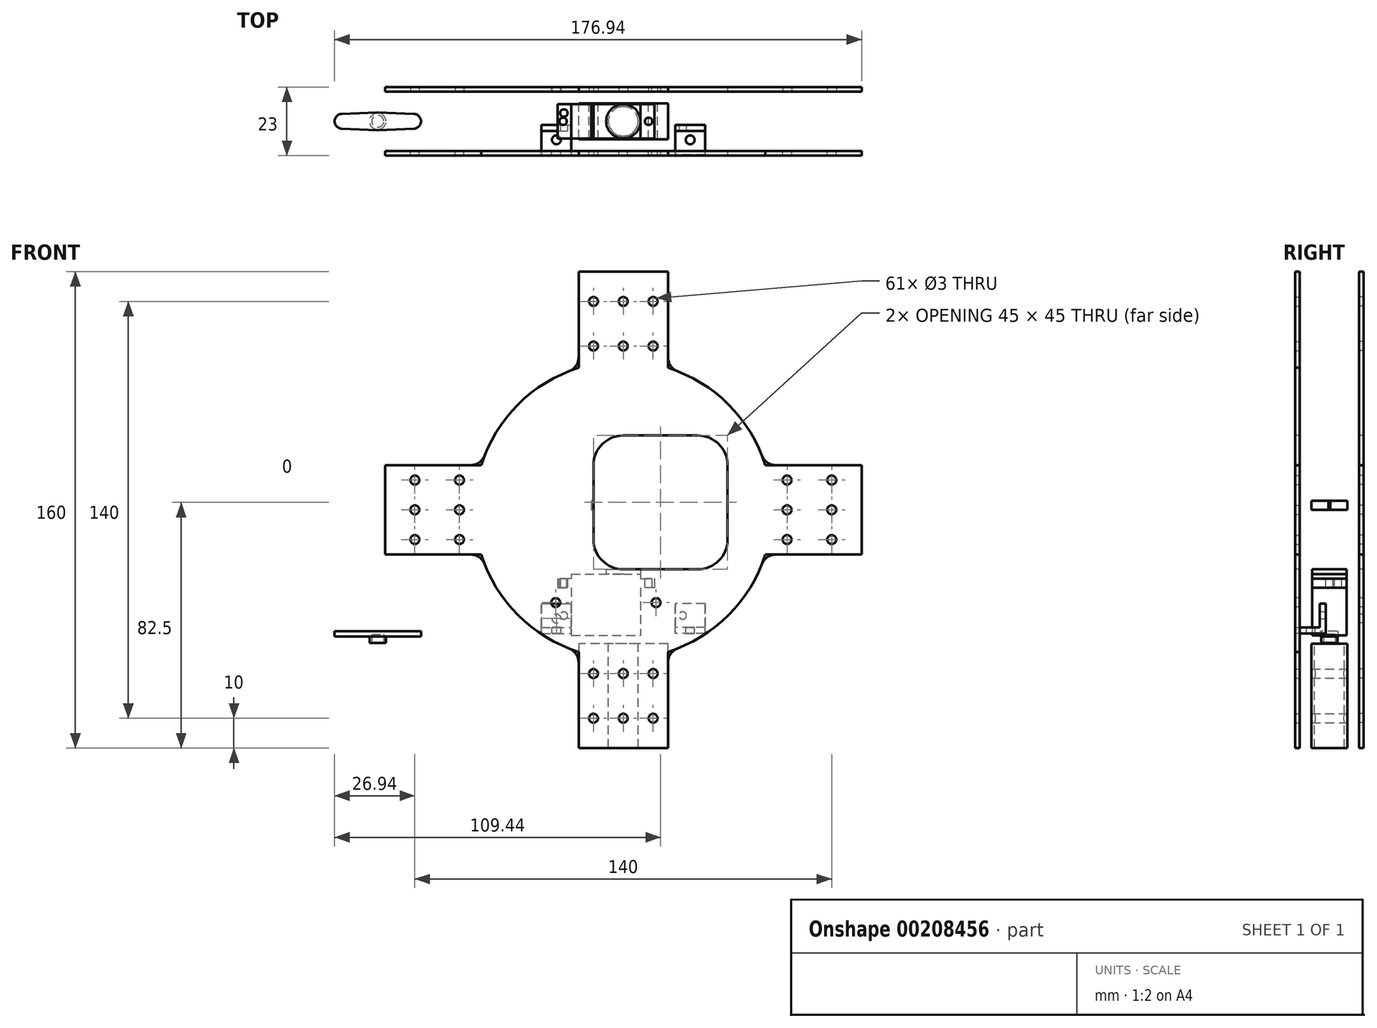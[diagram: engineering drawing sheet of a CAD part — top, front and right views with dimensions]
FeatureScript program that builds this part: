
annotation { "Feature Type Name" : "Feature", "Feature Type Description" : "" }
export const myFeature = defineFeature(function(context is Context, id is Id, definition is map)
    precondition{}
    {
        {
            var Q0;
            Q0=qCreatedBy(makeId("Top.planeOp"),FACE);
            var sketch = newSketch(context, id + "F0", { "sketchPlane" : qUnion([Q0])});
            skCircle(sketch, "E0", {"center": v(0, 0) * mm, "radius": 6 * mm});
            skLineSegment(sketch, "E1.bottom", {"start": v(-10.8, 6) * mm, "end": v(21.6, 6) * mm});
            skLineSegment(sketch, "E1.top", {"start": v(-10.8, -6) * mm, "end": v(21.6, -6) * mm});
            skLineSegment(sketch, "E1.left", {"start": v(-10.8, 6) * mm, "end": v(-10.8, -6) * mm});
            skLineSegment(sketch, "E1.right", {"start": v(21.6, 6) * mm, "end": v(21.6, -6) * mm});
            skCircle(sketch, "E2", {"center": v(-8.8, 0) * mm, "radius": 1.25 * mm});
            skCircle(sketch, "E3", {"center": v(19.6, 0) * mm, "radius": 1.25 * mm});
            skLineSegment(sketch, "E4", {"start": v(-6, 6) * mm, "end": v(-6, -6) * mm});
            skLineSegment(sketch, "E5", {"start": v(16.8, 6) * mm, "end": v(16.8, -6) * mm});
            skLineSegment(sketch, "E6", {"start": v(5.4, 6) * mm, "end": v(5.4, -6) * mm, "construction": true});
            skCircle(sketch, "E7", {"center": v(0, 0) * mm, "radius": 2 * mm});
            skSolve(sketch);
        }
        {
            var Q0;
            {var subQ5=sQuery(id+"F0.wireOp",EDGE,"E5");Q0=makeQuery(id+"F0.imprint","IMPRINT",FACE,{"disambiguationData":[TD([[makeQuery(id+"F0.imprint","IMPRINT",EDGE,{"derivedFrom":subQ5}),-1.0]])]});}
            var Q1;
            {var subQ0=sQuery(id+"F0.wireOp",EDGE,"E1.bottom");var subQ1=sQuery(id+"F0.wireOp",EDGE,"E0");var subQ2=makeQuery(id+"F0.imprint","INTERSECT",VERTEX,{"derivedFrom":[subQ1,subQ0]});Q1=makeQuery(id+"F0.imprint","IMPRINT",FACE,{"disambiguationData":[TD([[makeQuery(id+"F0.imprint","IMPRINT",EDGE,{"disambiguationData":[TD([[subQ2,-1.0]])],"derivedFrom":subQ1}),-1.0]])]});}
            var Q2;
            {var subQ0=sQuery(id+"F0.wireOp",EDGE,"E1.top");var subQ1=sQuery(id+"F0.wireOp",EDGE,"E0");var subQ2=makeQuery(id+"F0.imprint","INTERSECT",VERTEX,{"derivedFrom":[subQ1,subQ0]});Q2=makeQuery(id+"F0.imprint","IMPRINT",FACE,{"disambiguationData":[TD([[makeQuery(id+"F0.imprint","IMPRINT",EDGE,{"disambiguationData":[TD([[subQ2,1.0]])],"derivedFrom":subQ1}),-1.0]])]});}
            var Q3;
            {var subQ0=sQuery(id+"F0.wireOp",EDGE,"E0");var subQ1=makeQuery(id+"F0.imprint","INTERSECT",VERTEX,{"derivedFrom":[subQ0,sQuery(id+"F0.wireOp",EDGE,"E1.bottom")]});Q3=makeQuery(id+"F0.imprint","IMPRINT",FACE,{"disambiguationData":[TD([[makeQuery(id+"F0.imprint","IMPRINT",EDGE,{"disambiguationData":[TD([[subQ1,-1.0]])],"derivedFrom":subQ0}),1.0]])]});}
            var Q4;
            Q4=makeQuery(id+"F0.imprint","IMPRINT",FACE,{"disambiguationData":[TD([[makeQuery(id+"F0.imprint","IMPRINT",EDGE,{"derivedFrom":sQuery(id+"F0.wireOp",EDGE,"E7")}),1.0]])]});
            extrude(context, id + "F1", {"entities" : qUnion([Q0, Q1, Q2, Q3, Q4]), "oppositeDirection" : true, "depth" : 3 * mm});
        }
        {
            var Q0;
            {var subQ0=sQuery(id+"F0.wireOp",EDGE,"E1.left");Q0=makeQuery(id+"F0.imprint","IMPRINT",FACE,{"disambiguationData":[TD([[makeQuery(id+"F0.imprint","IMPRINT",EDGE,{"derivedFrom":subQ0}),1.0]])]});}
            var Q1;
            {var subQ0=sQuery(id+"F0.wireOp",EDGE,"E1.right");Q1=makeQuery(id+"F0.imprint","IMPRINT",FACE,{"disambiguationData":[TD([[makeQuery(id+"F0.imprint","IMPRINT",EDGE,{"derivedFrom":subQ0}),-1.0]])]});}
            var Q2;
            {var subQ5=sQuery(id+"F0.wireOp",EDGE,"E5");Q2=makeQuery(id+"F0.imprint","IMPRINT",FACE,{"disambiguationData":[TD([[makeQuery(id+"F0.imprint","IMPRINT",EDGE,{"derivedFrom":subQ5}),-1.0]])]});}
            var Q3;
            {var subQ0=sQuery(id+"F0.wireOp",EDGE,"E1.top");var subQ1=sQuery(id+"F0.wireOp",EDGE,"E0");var subQ2=makeQuery(id+"F0.imprint","INTERSECT",VERTEX,{"derivedFrom":[subQ1,subQ0]});Q3=makeQuery(id+"F0.imprint","IMPRINT",FACE,{"disambiguationData":[TD([[makeQuery(id+"F0.imprint","IMPRINT",EDGE,{"disambiguationData":[TD([[subQ2,1.0]])],"derivedFrom":subQ1}),-1.0]])]});}
            var Q4;
            {var subQ0=sQuery(id+"F0.wireOp",EDGE,"E0");var subQ1=makeQuery(id+"F0.imprint","INTERSECT",VERTEX,{"derivedFrom":[subQ0,sQuery(id+"F0.wireOp",EDGE,"E1.bottom")]});Q4=makeQuery(id+"F0.imprint","IMPRINT",FACE,{"disambiguationData":[TD([[makeQuery(id+"F0.imprint","IMPRINT",EDGE,{"disambiguationData":[TD([[subQ1,-1.0]])],"derivedFrom":subQ0}),1.0]])]});}
            var Q5;
            {var subQ0=sQuery(id+"F0.wireOp",EDGE,"E1.bottom");var subQ1=sQuery(id+"F0.wireOp",EDGE,"E0");var subQ2=makeQuery(id+"F0.imprint","INTERSECT",VERTEX,{"derivedFrom":[subQ1,subQ0]});Q5=makeQuery(id+"F0.imprint","IMPRINT",FACE,{"disambiguationData":[TD([[makeQuery(id+"F0.imprint","IMPRINT",EDGE,{"disambiguationData":[TD([[subQ2,-1.0]])],"derivedFrom":subQ1}),-1.0]])]});}
            var Q6;
            Q6=makeQuery(id+"F0.imprint","IMPRINT",FACE,{"disambiguationData":[TD([[makeQuery(id+"F0.imprint","IMPRINT",EDGE,{"derivedFrom":sQuery(id+"F0.wireOp",EDGE,"E7")}),1.0]])]});
            extrude(context, id + "F2", {"entities" : qUnion([Q0, Q1, Q2, Q3, Q4, Q5, Q6]), "operationType" : NewBodyOperationType.ADD, "depth" : 3 * mm});
        }
        {
            var Q0;
            {var subQ0=sQuery(id+"F0.wireOp",EDGE,"E0");var subQ1=makeQuery(id+"F0.imprint","INTERSECT",VERTEX,{"derivedFrom":[subQ0,sQuery(id+"F0.wireOp",EDGE,"E1.bottom")]});Q0=makeQuery(id+"F0.imprint","IMPRINT",FACE,{"disambiguationData":[TD([[makeQuery(id+"F0.imprint","IMPRINT",EDGE,{"disambiguationData":[TD([[subQ1,-1.0]])],"derivedFrom":subQ0}),1.0]])]});}
            var Q1;
            Q1=makeQuery(id+"F0.imprint","IMPRINT",FACE,{"disambiguationData":[TD([[makeQuery(id+"F0.imprint","IMPRINT",EDGE,{"derivedFrom":sQuery(id+"F0.wireOp",EDGE,"E7")}),1.0]])]});
            extrude(context, id + "F3", {"entities" : qUnion([Q0, Q1]), "operationType" : NewBodyOperationType.ADD, "depth" : (25.4 - 16.82) * mm});
        }
        {
            var Q0;
            Q0=qCreatedBy(makeId("Front.planeOp"),FACE);
            var sketch = newSketch(context, id + "F4", { "sketchPlane" : qUnion([Q0])});
            skLineSegment(sketch, "E8", {"start": v(-6, 3) * mm, "end": v(-6, 5.5) * mm});
            skLineSegment(sketch, "E9", {"start": v(-6, 5.5) * mm, "end": v(0, 7) * mm});
            skLineSegment(sketch, "E10", {"start": v(0, 7) * mm, "end": v(16.8, 3) * mm});
            skLineSegment(sketch, "E11", {"start": v(16.8, 3) * mm, "end": v(-6, 3) * mm});
            skSolve(sketch);
        }
        {
            var Q0;
            Q0 = qSketchRegion(id + "F4", true);
            var Q1;
            {var subQ0=sQuery(id+"F0.wireOp",EDGE,"E1.top");Q1=makeQuery(id+"F2.boolean.opBoolean","MERGE",FACE,{"derivedFrom":[makeQuery(id+"F1.opExtrude","SWEPT_FACE",FACE,{"disambiguationData":[OSD([subQ0])]}),makeQuery(id+"F2.opExtrude","SWEPT_FACE",FACE,{"disambiguationData":[OSD([subQ0])]})]});}
            var Q2;
            {var subQ0=sQuery(id+"F0.wireOp",EDGE,"E1.bottom");Q2=makeQuery(id+"F2.boolean.opBoolean","MERGE",FACE,{"derivedFrom":[makeQuery(id+"F1.opExtrude","SWEPT_FACE",FACE,{"disambiguationData":[OSD([subQ0])]}),makeQuery(id+"F2.opExtrude","SWEPT_FACE",FACE,{"disambiguationData":[OSD([subQ0])]})]});}
            extrude(context, id + "F5", {"entities" : qUnion([Q0]), "operationType" : NewBodyOperationType.ADD, "endBound" : BoundingType.UP_TO_SURFACE, "endBoundEntityFace" : qUnion([Q1]), "depth" : 25 * mm, "hasSecondDirection" : true, "secondDirectionBound" : SecondDirectionBoundingType.UP_TO_SURFACE, "secondDirectionOppositeDirection" : true, "secondDirectionBoundEntityFace" : qUnion([Q2]), "secondDirectionDepth" : 25 * mm});
        }
        {
            var Q0;
            Q0=makeQuery(id+"F0.imprint","IMPRINT",FACE,{"disambiguationData":[TD([[makeQuery(id+"F0.imprint","IMPRINT",EDGE,{"derivedFrom":sQuery(id+"F0.wireOp",EDGE,"E7")}),1.0]])]});
            extrude(context, id + "F6", {"entities" : qUnion([Q0]), "operationType" : NewBodyOperationType.ADD, "depth" : 11.48 * mm});
        }
        {
            var Q0;
            Q0=makeQuery(id+"F2.opExtrude","SWEPT_EDGE",EDGE,{"disambiguationData":[OSD([sQuery(id+"F0.wireOp",EDGE,"E1.top"),sQuery(id+"F0.wireOp",EDGE,"E1.right")])]});
            var Q1;
            Q1=makeQuery(id+"F1.opExtrude","SWEPT_EDGE",EDGE,{"disambiguationData":[OSD([sQuery(id+"F0.wireOp",EDGE,"E1.top"),sQuery(id+"F0.wireOp",EDGE,"E5")])]});
            var Q2;
            Q2=makeQuery(id+"F2.opExtrude","SWEPT_EDGE",EDGE,{"disambiguationData":[OSD([sQuery(id+"F0.wireOp",EDGE,"E1.bottom"),sQuery(id+"F0.wireOp",EDGE,"E1.right")])]});
            var Q3;
            Q3=makeQuery(id+"F1.opExtrude","SWEPT_EDGE",EDGE,{"disambiguationData":[OSD([sQuery(id+"F0.wireOp",EDGE,"E1.bottom"),sQuery(id+"F0.wireOp",EDGE,"E5")])]});
            var Q4;
            Q4=makeQuery(id+"F1.opExtrude","SWEPT_EDGE",EDGE,{"disambiguationData":[OSD([sQuery(id+"F0.wireOp",EDGE,"E1.top"),sQuery(id+"F0.wireOp",EDGE,"E4")])]});
            var Q5;
            {var subQ0=sQuery(id+"F0.wireOp",EDGE,"E1.top");Q5=makeQuery(id+"F5.opExtrude","TWEAK_EDGE",EDGE,{"derivedFrom":[makeQuery(id+"F2.boolean.opBoolean","MERGE",FACE,{"derivedFrom":[makeQuery(id+"F1.opExtrude","SWEPT_FACE",FACE,{"disambiguationData":[OSD([subQ0])]}),makeQuery(id+"F2.opExtrude","SWEPT_FACE",FACE,{"disambiguationData":[OSD([subQ0])]})]}),makeQuery(id+"F4.imprint","IMPRINT",EDGE,{"derivedFrom":sQuery(id+"F4.wireOp",EDGE,"E8")})]});}
            var Q6;
            Q6=makeQuery(id+"F2.opExtrude","SWEPT_EDGE",EDGE,{"disambiguationData":[OSD([sQuery(id+"F0.wireOp",EDGE,"E1.top"),sQuery(id+"F0.wireOp",EDGE,"E1.left")])]});
            var Q7;
            Q7=makeQuery(id+"F2.opExtrude","SWEPT_EDGE",EDGE,{"disambiguationData":[OSD([sQuery(id+"F0.wireOp",EDGE,"E1.bottom"),sQuery(id+"F0.wireOp",EDGE,"E1.left")])]});
            var Q8;
            Q8=makeQuery(id+"F1.opExtrude","SWEPT_EDGE",EDGE,{"disambiguationData":[OSD([sQuery(id+"F0.wireOp",EDGE,"E1.bottom"),sQuery(id+"F0.wireOp",EDGE,"E4")])]});
            var Q9;
            {var subQ0=sQuery(id+"F0.wireOp",EDGE,"E1.bottom");Q9=makeQuery(id+"F5.opExtrude","TWEAK_EDGE",EDGE,{"derivedFrom":[makeQuery(id+"F2.boolean.opBoolean","MERGE",FACE,{"derivedFrom":[makeQuery(id+"F1.opExtrude","SWEPT_FACE",FACE,{"disambiguationData":[OSD([subQ0])]}),makeQuery(id+"F2.opExtrude","SWEPT_FACE",FACE,{"disambiguationData":[OSD([subQ0])]})]}),makeQuery(id+"F4.imprint","IMPRINT",EDGE,{"derivedFrom":sQuery(id+"F4.wireOp",EDGE,"E8")})]});}
            fillet(context, id + "F7", {"entities" : qUnion([Q0, Q1, Q2, Q3, Q4, Q5, Q6, Q7, Q8, Q9]), "radius" : 0.5 * mm, "tangentPropagation" : true, "allowEdgeOverflow" : false});
        }
        {
            var Q0;
            Q0=makeQuery(id+"F1.opExtrude","CAP_FACE",FACE,{"disambiguationData":[OSD([sQuery(id+"F0.wireOp",EDGE,"E1.bottom"),sQuery(id+"F0.wireOp",EDGE,"E1.top"),sQuery(id+"F0.wireOp",EDGE,"E4"),sQuery(id+"F0.wireOp",EDGE,"E5")])],"isStart":false});
            extrude(context, id + "F8", {"entities" : qUnion([Q0]), "operationType" : NewBodyOperationType.ADD, "depth" : 10.82 * mm});
        }
        {
            var Q0;
            Q0=makeQuery(id+"F8.opExtrude","CAP_FACE",FACE,{"disambiguationData":[OSD([sQuery(id+"F0.wireOp",EDGE,"E1.bottom"),sQuery(id+"F0.wireOp",EDGE,"E1.top"),sQuery(id+"F0.wireOp",EDGE,"E4"),sQuery(id+"F0.wireOp",EDGE,"E5")])],"isStart":false});
            extrude(context, id + "F9", {"entities" : qUnion([Q0]), "operationType" : NewBodyOperationType.ADD, "depth" : 3 * mm});
        }
        {
            var Q0;
            {var subQ0=sQuery(id+"F0.wireOp",EDGE,"E4");Q0=makeQuery(id+"F9.boolean.opBoolean","MERGE",FACE,{"derivedFrom":[makeQuery(id+"F8.boolean.opBoolean","MERGE",FACE,{"derivedFrom":[makeQuery(id+"F1.opExtrude","SWEPT_FACE",FACE,{"disambiguationData":[OSD([subQ0])]}),makeQuery(id+"F8.opExtrude","SWEPT_FACE",FACE,{"disambiguationData":[OSD([subQ0])]})]}),makeQuery(id+"F9.opExtrude","SWEPT_FACE",FACE,{"disambiguationData":[OSD([subQ0])]})]});}
            var sketch = newSketch(context, id + "F10", { "sketchPlane" : qUnion([Q0])});
            skLineSegment(sketch, "E12.bottom", {"start": v(-2.5, -16.82) * mm, "end": v(2.5, -16.82) * mm});
            skLineSegment(sketch, "E12.top", {"start": v(-2.5, -15.82) * mm, "end": v(2.5, -15.82) * mm});
            skLineSegment(sketch, "E12.left", {"start": v(-2.5, -16.82) * mm, "end": v(-2.5, -15.82) * mm});
            skLineSegment(sketch, "E12.right", {"start": v(2.5, -16.82) * mm, "end": v(2.5, -15.82) * mm});
            skSolve(sketch);
        }
        {
            var Q0;
            Q0 = qSketchRegion(id + "F10", true);
            extrude(context, id + "F11", {"entities" : qUnion([Q0]), "operationType" : NewBodyOperationType.ADD, "depth" : 3 * mm});
        }
        {
            var Q0;
            Q0=qCreatedBy(makeId("Front.planeOp"),FACE);
            var sketch = newSketch(context, id + "F12", { "sketchPlane" : qUnion([Q0])});
            skLineSegment(sketch, "E13", {"start": v(0, 12.98) * mm, "end": v(10, 12.98) * mm});
            skLineSegment(sketch, "E14", {"start": v(10, 12.98) * mm, "end": v(10, 11.48) * mm});
            skLineSegment(sketch, "E15", {"start": v(10, 11.48) * mm, "end": v(3, 11.48) * mm});
            skLineSegment(sketch, "E16", {"start": v(3, 11.48) * mm, "end": v(3, 8.98) * mm});
            skLineSegment(sketch, "E17", {"start": v(3, 8.98) * mm, "end": v(2, 8.98) * mm});
            skLineSegment(sketch, "E18", {"start": v(2, 8.98) * mm, "end": v(2, 11.48) * mm});
            skLineSegment(sketch, "E19", {"start": v(2, 11.48) * mm, "end": v(0, 11.48) * mm});
            skLineSegment(sketch, "E20", {"start": v(0, 11.48) * mm, "end": v(0, 12.98) * mm});
            skSolve(sketch);
        }
        {
            var Q0;
            Q0=makeQuery(id+"F12.imprint","IMPRINT",FACE,{"disambiguationData":[TD([[makeQuery(id+"F12.imprint","IMPRINT",EDGE,{"derivedFrom":sQuery(id+"F12.wireOp",EDGE,"E13")}),-1.0]])]});
            var Q1;
            Q1=sQuery(id+"F12.wireOp",EDGE,"E20");
            revolve(context, id + "F13", {"entities" : qUnion([Q0]), "axis" : qUnion([Q1]), "revolveType" : RevolveType.FULL});
        }
        {
            var Q0;
            Q0=qCreatedBy(makeId("Front.planeOp"),FACE);
            var sketch = newSketch(context, id + "F14", { "sketchPlane" : qUnion([Q0])});
            skLineSegment(sketch, "E21.bottom", {"start": v(-17.45, -21.65) * mm, "end": v(5.75, -21.65) * mm});
            skLineSegment(sketch, "E21.top", {"start": v(-17.45, -42.15) * mm, "end": v(5.75, -42.15) * mm});
            skLineSegment(sketch, "E21.left", {"start": v(-17.45, -21.65) * mm, "end": v(-17.45, -42.15) * mm});
            skLineSegment(sketch, "E21.right", {"start": v(5.75, -21.65) * mm, "end": v(5.75, -42.15) * mm});
            skLineSegment(sketch, "E22", {"start": v(-17.45, -23.15) * mm, "end": v(-22.1, -23.15) * mm});
            skLineSegment(sketch, "E23", {"start": v(-22.1, -23.15) * mm, "end": v(-22.1, -26.15) * mm});
            skLineSegment(sketch, "E24", {"start": v(-22.1, -26.15) * mm, "end": v(-17.45, -26.15) * mm});
            skLineSegment(sketch, "E25", {"start": v(5.75, -23.15) * mm, "end": v(10.4, -23.15) * mm});
            skLineSegment(sketch, "E26", {"start": v(10.4, -23.15) * mm, "end": v(10.4, -26.15) * mm});
            skLineSegment(sketch, "E27", {"start": v(10.4, -26.15) * mm, "end": v(5.75, -26.15) * mm});
            skSolve(sketch);
        }
        {
            var Q0;
            {var subQ4=sQuery(id+"F14.wireOp",EDGE,"E21.bottom");Q0=makeQuery(id+"F14.imprint","IMPRINT",FACE,{"disambiguationData":[TD([[makeQuery(id+"F14.imprint","IMPRINT",EDGE,{"derivedFrom":subQ4}),-1.0]])]});}
            var Q1;
            {var subQ0=sQuery(id+"F14.wireOp",EDGE,"E22");Q1=makeQuery(id+"F14.imprint","IMPRINT",FACE,{"disambiguationData":[TD([[makeQuery(id+"F14.imprint","IMPRINT",EDGE,{"derivedFrom":subQ0}),1.0]])]});}
            var Q2;
            {var subQ0=sQuery(id+"F14.wireOp",EDGE,"E25");Q2=makeQuery(id+"F14.imprint","IMPRINT",FACE,{"disambiguationData":[TD([[makeQuery(id+"F14.imprint","IMPRINT",EDGE,{"derivedFrom":subQ0}),-1.0]])]});}
            extrude(context, id + "F15", {"entities" : qUnion([Q0, Q1, Q2]), "endBound" : BoundingType.SYMMETRIC, "depth" : 11.5 * mm});
        }
        {
            var Q0;
            Q0=makeQuery(id+"F15.opExtrude","SWEPT_FACE",FACE,{"disambiguationData":[OSD([sQuery(id+"F14.wireOp",EDGE,"E21.bottom")])]});
            var sketch = newSketch(context, id + "F16", { "sketchPlane" : qUnion([Q0])});
            skLineSegment(sketch, "E28", {"start": v(-5.85, 5.75) * mm, "end": v(-5.85, -5.75) * mm, "construction": true});
            skCircle(sketch, "E29", {"center": v(-20.2, 0) * mm, "radius": 1.25 * mm});
            skCircle(sketch, "E30", {"center": v(8.5, 0) * mm, "radius": 1.25 * mm});
            skCircle(sketch, "E31", {"center": v(0, 0) * mm, "radius": 5.75 * mm});
            skCircle(sketch, "E32", {"center": v(0, 0) * mm, "radius": 2 * mm});
            skSolve(sketch);
        }
        {
            var Q0;
            Q0=makeQuery(id+"F16.imprint","IMPRINT",FACE,{"disambiguationData":[TD([[makeQuery(id+"F16.imprint","IMPRINT",EDGE,{"derivedFrom":sQuery(id+"F16.wireOp",EDGE,"E32")}),-1.0]])]});
            var Q1;
            Q1=makeQuery(id+"F16.imprint","IMPRINT",FACE,{"disambiguationData":[TD([[makeQuery(id+"F16.imprint","IMPRINT",EDGE,{"derivedFrom":sQuery(id+"F16.wireOp",EDGE,"E32")}),1.0]])]});
            extrude(context, id + "F17", {"entities" : qUnion([Q0, Q1]), "operationType" : NewBodyOperationType.ADD, "depth" : 4.5 * mm});
        }
        {
            var Q0;
            Q0=makeQuery(id+"F16.imprint","IMPRINT",FACE,{"disambiguationData":[TD([[makeQuery(id+"F16.imprint","IMPRINT",EDGE,{"derivedFrom":sQuery(id+"F16.wireOp",EDGE,"E32")}),1.0]])]});
            extrude(context, id + "F18", {"entities" : qUnion([Q0]), "operationType" : NewBodyOperationType.ADD, "depth" : 7.3 * mm});
        }
        {
            var Q0;
            Q0=makeQuery(id+"F16.imprint","IMPRINT",FACE,{"disambiguationData":[TD([[makeQuery(id+"F16.imprint","IMPRINT",EDGE,{"derivedFrom":sQuery(id+"F16.wireOp",EDGE,"E29")}),1.0]])]});
            var Q1;
            Q1=makeQuery(id+"F16.imprint","IMPRINT",FACE,{"disambiguationData":[TD([[makeQuery(id+"F16.imprint","IMPRINT",EDGE,{"derivedFrom":sQuery(id+"F16.wireOp",EDGE,"E30")}),1.0]])]});
            extrude(context, id + "F19", {"entities" : qUnion([Q0, Q1]), "operationType" : NewBodyOperationType.REMOVE, "oppositeDirection" : true, "depth" : 25 * mm});
        }
        {
            var Q0;
            Q0=qCreatedBy(makeId("Front.planeOp"),FACE);
            var sketch = newSketch(context, id + "F20", { "sketchPlane" : qUnion([Q0])});
            skLineSegment(sketch, "E33", {"start": v(2, -14.35) * mm, "end": v(2, -17.15) * mm});
            skLineSegment(sketch, "E34", {"start": v(-2, -17.15) * mm, "end": v(-2, -14.35) * mm});
            skLineSegment(sketch, "E35", {"start": v(-2, -17.15) * mm, "end": v(-2, -14.15) * mm});
            skPoint(sketch, "E35.endSnap0", {"position": v(-2, -15.75) * mm});
            skLineSegment(sketch, "E36", {"start": v(-2, -14.15) * mm, "end": v(0, -14.15) * mm});
            skLineSegment(sketch, "E37", {"start": v(0, -14.15) * mm, "end": v(0, -13.65) * mm});
            skLineSegment(sketch, "E38", {"start": v(0, -13.65) * mm, "end": v(-8, -13.65) * mm});
            skLineSegment(sketch, "E39", {"start": v(-8, -13.65) * mm, "end": v(-8, -14.85) * mm});
            skLineSegment(sketch, "E40", {"start": v(-8, -14.85) * mm, "end": v(-2.75, -14.85) * mm});
            skLineSegment(sketch, "E41", {"start": v(-2.75, -14.85) * mm, "end": v(-2.75, -17.15) * mm});
            skLineSegment(sketch, "E42", {"start": v(-2.75, -17.15) * mm, "end": v(-2, -17.15) * mm});
            skSolve(sketch);
        }
        {
            var Q0;
            {var subQ0=sQuery(id+"F20.wireOp",EDGE,"E36");Q0=makeQuery(id+"F20.imprint","IMPRINT",FACE,{"disambiguationData":[TD([[makeQuery(id+"F20.imprint","IMPRINT",EDGE,{"derivedFrom":subQ0}),1.0]])]});}
            var Q1;
            Q1=sQuery(id+"F20.wireOp",EDGE,"E37");
            revolve(context, id + "F21", {"entities" : qUnion([Q0]), "axis" : qUnion([Q1]), "revolveType" : RevolveType.FULL});
        }
        {
            var Q0;
            Q0=qCreatedBy(makeId("Front.planeOp"),FACE);
            var sketch = newSketch(context, id + "F22", { "sketchPlane" : qUnion([Q0])});
            skLineSegment(sketch, "E43", {"start": v(-8, -11.65) * mm, "end": v(-8, -13.65) * mm});
            skLineSegment(sketch, "E44", {"start": v(-8, -13.65) * mm, "end": v(17, -13.65) * mm});
            skLineSegment(sketch, "E45", {"start": v(17, -13.65) * mm, "end": v(17, 23.35) * mm});
            skLineSegment(sketch, "E46", {"start": v(17, 23.35) * mm, "end": v(15, 23.35) * mm});
            skLineSegment(sketch, "E47", {"start": v(15, 23.35) * mm, "end": v(15, -11.65) * mm});
            skLineSegment(sketch, "E48", {"start": v(15, -11.65) * mm, "end": v(-8, -11.65) * mm});
            skSolve(sketch);
        }
        {
            var Q0;
            Q0=makeQuery(id+"F22.imprint","IMPRINT",FACE,{"disambiguationData":[TD([[makeQuery(id+"F22.imprint","IMPRINT",EDGE,{"derivedFrom":sQuery(id+"F22.wireOp",EDGE,"E43")}),1.0]])]});
            extrude(context, id + "F23", {"entities" : qUnion([Q0]), "endBound" : BoundingType.SYMMETRIC, "depth" : 16 * mm});
        }
        {
            var Q0;
            Q0=makeQuery(id+"F23.opExtrude","SWEPT_FACE",FACE,{"disambiguationData":[OSD([sQuery(id+"F22.wireOp",EDGE,"E47")])]});
            var sketch = newSketch(context, id + "F24", { "sketchPlane" : qUnion([Q0])});
            skLineSegment(sketch, "E49.bottom", {"start": v(-6, 17.6) * mm, "end": v(6, 17.6) * mm});
            skLineSegment(sketch, "E49.top", {"start": v(-6, -5.9) * mm, "end": v(6, -5.9) * mm});
            skLineSegment(sketch, "E49.left", {"start": v(-6, 17.6) * mm, "end": v(-6, -5.9) * mm});
            skLineSegment(sketch, "E49.right", {"start": v(6, 17.6) * mm, "end": v(6, -5.9) * mm});
            skLineSegment(sketch, "E50", {"start": v(-8, 5.85) * mm, "end": v(8, 5.85) * mm, "construction": true});
            skCircle(sketch, "E51", {"center": v(0, 20.2) * mm, "radius": 1.25 * mm});
            skCircle(sketch, "E52.MirrorC", {"center": v(0, -8.5) * mm, "radius": 1.25 * mm});
            skCircle(sketch, "E53", {"center": v(0, 0) * mm, "radius": 5.75 * mm, "construction": true});
            skLineSegment(sketch, "E54.bottom", {"start": v(-5.75, -5.75) * mm, "end": v(5.75, -5.75) * mm, "construction": true});
            skLineSegment(sketch, "E54.top", {"start": v(-5.75, 17.45) * mm, "end": v(5.75, 17.45) * mm, "construction": true});
            skLineSegment(sketch, "E54.left", {"start": v(-5.75, -5.75) * mm, "end": v(-5.75, 17.45) * mm, "construction": true});
            skLineSegment(sketch, "E54.right", {"start": v(5.75, -5.75) * mm, "end": v(5.75, 17.45) * mm, "construction": true});
            skSolve(sketch);
        }
        {
            var Q0;
            Q0 = qSketchRegion(id + "F24", true);
            var Q1;
            Q1=makeQuery(id+"F23.opExtrude","SWEPT_FACE",FACE,{"disambiguationData":[OSD([sQuery(id+"F22.wireOp",EDGE,"E45")])]});
            extrude(context, id + "F25", {"entities" : qUnion([Q0]), "operationType" : NewBodyOperationType.REMOVE, "endBound" : BoundingType.UP_TO_SURFACE, "oppositeDirection" : true, "endBoundEntityFace" : qUnion([Q1]), "depth" : 25 * mm});
        }
        {
            var Q0;
            Q0=makeQuery(id+"F23.opExtrude","SWEPT_FACE",FACE,{"disambiguationData":[OSD([sQuery(id+"F22.wireOp",EDGE,"E48")])]});
            var sketch = newSketch(context, id + "F26", { "sketchPlane" : qUnion([Q0])});
            skCircle(sketch, "E55", {"center": v(0, 0) * mm, "radius": 1 * mm});
            skCircle(sketch, "E56", {"center": v(6, 0) * mm, "radius": 0.75 * mm});
            skCircle(sketch, "E57", {"center": v(-6, 0) * mm, "radius": 0.75 * mm});
            skLineSegment(sketch, "E58", {"start": v(0, -1) * mm, "end": v(0, 1) * mm, "construction": true});
            skCircle(sketch, "E59", {"center": v(0, -6) * mm, "radius": 0.75 * mm});
            skCircle(sketch, "E60", {"center": v(0, 6) * mm, "radius": 0.75 * mm});
            skSolve(sketch);
        }
        {
            var Q0;
            Q0 = qSketchRegion(id + "F26", true);
            var Q1;
            Q1=makeQuery(id+"F23.opExtrude","SWEPT_FACE",FACE,{"disambiguationData":[OSD([sQuery(id+"F22.wireOp",EDGE,"E44")])]});
            extrude(context, id + "F27", {"entities" : qUnion([Q0]), "operationType" : NewBodyOperationType.REMOVE, "endBound" : BoundingType.UP_TO_SURFACE, "oppositeDirection" : true, "endBoundEntityFace" : qUnion([Q1]), "depth" : 25 * mm});
        }
        {
            var Q0;
            Q0=makeQuery(id+"F23.opExtrude","CAP_EDGE",EDGE,{"disambiguationData":[OSD([sQuery(id+"F22.wireOp",EDGE,"E46")])],"isStart":false});
            var Q1;
            Q1=makeQuery(id+"F23.opExtrude","CAP_EDGE",EDGE,{"disambiguationData":[OSD([sQuery(id+"F22.wireOp",EDGE,"E46")])],"isStart":true});
            var Q2;
            Q2=makeQuery(id+"F23.opExtrude","CAP_EDGE",EDGE,{"disambiguationData":[OSD([sQuery(id+"F22.wireOp",EDGE,"E43")])],"isStart":true});
            var Q3;
            Q3=makeQuery(id+"F23.opExtrude","CAP_EDGE",EDGE,{"disambiguationData":[OSD([sQuery(id+"F22.wireOp",EDGE,"E43")])],"isStart":false});
            fillet(context, id + "F28", {"entities" : qUnion([Q0, Q1, Q2, Q3]), "radius" : 5 * mm, "tangentPropagation" : true, "allowEdgeOverflow" : false});
        }
        {
            var Q0;
            Q0=qCreatedBy(makeId("Front.planeOp"),FACE);
            var sketch = newSketch(context, id + "F29", { "sketchPlane" : qUnion([Q0])});
            skCircle(sketch, "E61", {"center": v(0, 0) * mm, "radius": 50 * mm, "construction": true});
            skLineSegment(sketch, "E62", {"start": v(15, 21.45) * mm, "end": v(17, 21.45) * mm, "construction": true});
            skLineSegment(sketch, "E63", {"start": v(17, 18.95) * mm, "end": v(15, 18.95) * mm, "construction": true});
            skCircle(sketch, "E64", {"center": v(0, 0) * mm, "radius": 80 * mm});
            skLineSegment(sketch, "E65", {"start": v(15, -78.58) * mm, "end": v(15, -45) * mm});
            skLineSegment(sketch, "E66", {"start": v(15, -45) * mm, "end": v(-15, -45) * mm});
            skLineSegment(sketch, "E67", {"start": v(-15, -45) * mm, "end": v(-15, -78.58) * mm});
            skLineSegment(sketch, "E68", {"start": v(-5, -79.84) * mm, "end": v(-5, -45) * mm, "construction": true});
            skLineSegment(sketch, "E69", {"start": v(5, -79.84) * mm, "end": v(5, -45) * mm, "construction": true});
            skCircle(sketch, "E70", {"center": v(-10, -70) * mm, "radius": 1.5 * mm});
            skCircle(sketch, "E71.0.1.0", {"center": v(-10, -55) * mm, "radius": 1.5 * mm});
            skCircle(sketch, "E71.1.0.0", {"center": v(0, -70) * mm, "radius": 1.5 * mm});
            skCircle(sketch, "E71.1.1.0", {"center": v(0, -55) * mm, "radius": 1.5 * mm});
            skCircle(sketch, "E71.2.0.0", {"center": v(10, -70) * mm, "radius": 1.5 * mm});
            skCircle(sketch, "E71.2.1.0", {"center": v(10, -55) * mm, "radius": 1.5 * mm});
            skLineSegment(sketch, "E71.direction1", {"start": v(-10, -70) * mm, "end": v(0, -70) * mm, "construction": true});
            skLineSegment(sketch, "E71.direction2", {"start": v(-10, -70) * mm, "end": v(-10, -55) * mm, "construction": true});
            skCircle(sketch, "E72.1.0", {"center": v(70, 10) * mm, "radius": 1.5 * mm});
            skCircle(sketch, "E72.1.1", {"center": v(55, 10) * mm, "radius": 1.5 * mm});
            skCircle(sketch, "E72.1.2", {"center": v(70, 0) * mm, "radius": 1.5 * mm});
            skCircle(sketch, "E72.1.3", {"center": v(55, 0) * mm, "radius": 1.5 * mm});
            skCircle(sketch, "E72.1.4", {"center": v(70, -10) * mm, "radius": 1.5 * mm});
            skCircle(sketch, "E72.1.5", {"center": v(55, -10) * mm, "radius": 1.5 * mm});
            skCircle(sketch, "E72.2.0", {"center": v(-10, 70) * mm, "radius": 1.5 * mm});
            skCircle(sketch, "E72.2.1", {"center": v(-10, 55) * mm, "radius": 1.5 * mm});
            skCircle(sketch, "E72.2.2", {"center": v(0, 70) * mm, "radius": 1.5 * mm});
            skCircle(sketch, "E72.2.3", {"center": v(0, 55) * mm, "radius": 1.5 * mm});
            skCircle(sketch, "E72.2.4", {"center": v(10, 70) * mm, "radius": 1.5 * mm});
            skCircle(sketch, "E72.2.5", {"center": v(10, 55) * mm, "radius": 1.5 * mm});
            skCircle(sketch, "E72.3.0", {"center": v(-70, -10) * mm, "radius": 1.5 * mm});
            skCircle(sketch, "E72.3.1", {"center": v(-55, -10) * mm, "radius": 1.5 * mm});
            skCircle(sketch, "E72.3.2", {"center": v(-70, 0) * mm, "radius": 1.5 * mm});
            skCircle(sketch, "E72.3.3", {"center": v(-55, 0) * mm, "radius": 1.5 * mm});
            skCircle(sketch, "E72.3.4", {"center": v(-70, 10) * mm, "radius": 1.5 * mm});
            skCircle(sketch, "E72.3.5", {"center": v(-55, 10) * mm, "radius": 1.5 * mm});
            skLineSegment(sketch, "E73.bottom", {"start": v(80, 80) * mm, "end": v(-80, 80) * mm});
            skLineSegment(sketch, "E73.top", {"start": v(80, -80) * mm, "end": v(-80, -80) * mm});
            skLineSegment(sketch, "E73.left", {"start": v(80, 80) * mm, "end": v(80, -80) * mm});
            skLineSegment(sketch, "E73.right", {"start": v(-80, 80) * mm, "end": v(-80, -80) * mm});
            skLineSegment(sketch, "E74", {"start": v(15, -78.58) * mm, "end": v(15, -80) * mm});
            skLineSegment(sketch, "E75", {"start": v(-15, -78.58) * mm, "end": v(-15, -80) * mm});
            skSolve(sketch);
        }
        {
            var Q0;
            Q0=makeQuery(id+"F29.imprint","IMPRINT",FACE,{"disambiguationData":[TD([[makeQuery(id+"F29.imprint","IMPRINT",EDGE,{"derivedFrom":sQuery(id+"F29.wireOp",EDGE,"E64")}),1.0]])]});
            var Q1;
            Q1=makeQuery(id+"F29.imprint","IMPRINT",FACE,{"disambiguationData":[TD([[makeQuery(id+"F29.imprint","IMPRINT",EDGE,{"derivedFrom":sQuery(id+"F29.wireOp",EDGE,"uRIWM3SE-HjLF-7pp9-PAPw-X7moghJSHD6N")}),-1.0]])]});
            var Q2;
            {var subQ0=sQuery(id+"F29.wireOp",EDGE,"E65");Q2=makeQuery(id+"F29.imprint","IMPRINT",FACE,{"disambiguationData":[TD([[makeQuery(id+"F29.imprint","IMPRINT",EDGE,{"derivedFrom":subQ0}),1.0]])]});}
            var Q3;
            {var subQ4=sQuery(id+"F29.wireOp",EDGE,"6Y47HZDB-cD7Z-lsIU-wivC-G1rU3xkXcbP8");Q3=makeQuery(id+"F29.imprint","IMPRINT",FACE,{"disambiguationData":[TD([[makeQuery(id+"F29.imprint","IMPRINT",EDGE,{"derivedFrom":subQ4}),1.0]])]});}
            var Q4;
            {var subQ3=sQuery(id+"F29.wireOp",EDGE,"AgJOStj8-b7i0-9NHD-Wp1m-9V2MUWHPPAkM");Q4=makeQuery(id+"F29.imprint","IMPRINT",FACE,{"disambiguationData":[TD([[makeQuery(id+"F29.imprint","IMPRINT",EDGE,{"derivedFrom":subQ3}),-1.0]])]});}
            var Q5;
            {var subQ3=sQuery(id+"F29.wireOp",EDGE,"WGm4aKHV-mp4h-Ylfv-BJxi-OSG1QRuU1NWU");Q5=makeQuery(id+"F29.imprint","IMPRINT",FACE,{"disambiguationData":[TD([[makeQuery(id+"F29.imprint","IMPRINT",EDGE,{"derivedFrom":subQ3}),-1.0]])]});}
            var Q6;
            {var subQ0=sQuery(id+"F29.wireOp",EDGE,"E65");Q6=makeQuery(id+"F29.imprint","IMPRINT",FACE,{"disambiguationData":[TD([[makeQuery(id+"F29.imprint","IMPRINT",EDGE,{"derivedFrom":subQ0}),-1.0]])]});}
            var Q7;
            {var subQ0=sQuery(id+"F29.wireOp",EDGE,"E73.bottom");var subQ1=sQuery(id+"F29.wireOp",EDGE,"E64");var subQ2=makeQuery(id+"F29.imprint","INTERSECT",VERTEX,{"derivedFrom":[subQ1,subQ0]});Q7=makeQuery(id+"F29.imprint","IMPRINT",FACE,{"disambiguationData":[TD([[makeQuery(id+"F29.imprint","IMPRINT",EDGE,{"disambiguationData":[TD([[subQ2,1.0]])],"derivedFrom":subQ1}),-1.0]])]});}
            var Q8;
            {var subQ0=sQuery(id+"F29.wireOp",EDGE,"E64");var subQ1=makeQuery(id+"F29.imprint","INTERSECT",VERTEX,{"derivedFrom":[subQ0,sQuery(id+"F29.wireOp",EDGE,"E65")]});Q8=makeQuery(id+"F29.imprint","IMPRINT",FACE,{"disambiguationData":[TD([[makeQuery(id+"F29.imprint","IMPRINT",EDGE,{"disambiguationData":[TD([[subQ1,1.0]])],"derivedFrom":subQ0}),-1.0]])]});}
            var Q9;
            {var subQ0=sQuery(id+"F29.wireOp",EDGE,"E73.bottom");var subQ1=sQuery(id+"F29.wireOp",EDGE,"E64");var subQ2=makeQuery(id+"F29.imprint","INTERSECT",VERTEX,{"derivedFrom":[subQ1,subQ0]});Q9=makeQuery(id+"F29.imprint","IMPRINT",FACE,{"disambiguationData":[TD([[makeQuery(id+"F29.imprint","IMPRINT",EDGE,{"disambiguationData":[TD([[subQ2,-1.0]])],"derivedFrom":subQ1}),-1.0]])]});}
            var Q10;
            {var subQ0=sQuery(id+"F29.wireOp",EDGE,"E75");Q10=makeQuery(id+"F29.imprint","IMPRINT",FACE,{"disambiguationData":[TD([[makeQuery(id+"F29.imprint","IMPRINT",EDGE,{"derivedFrom":subQ0}),1.0]])]});}
            var Q11;
            {var subQ0=sQuery(id+"F29.wireOp",EDGE,"E74");Q11=makeQuery(id+"F29.imprint","IMPRINT",FACE,{"disambiguationData":[TD([[makeQuery(id+"F29.imprint","IMPRINT",EDGE,{"derivedFrom":subQ0}),1.0]])]});}
            var Q12;
            {var subQ0=sQuery(id+"F29.wireOp",EDGE,"E75");Q12=makeQuery(id+"F29.imprint","IMPRINT",FACE,{"disambiguationData":[TD([[makeQuery(id+"F29.imprint","IMPRINT",EDGE,{"derivedFrom":subQ0}),-1.0]])]});}
            extrude(context, id + "F30", {"entities" : qUnion([Q0, Q1, Q2, Q3, Q4, Q5, Q6, Q7, Q8, Q9, Q10, Q11, Q12]), "depth" : 11.5 * mm, "hasSecondDirection" : true, "secondDirectionOppositeDirection" : false, "secondDirectionDepth" : 10 * mm});
        }
        {
            var Q0;
            Q0=makeQuery(id+"F30.opExtrude","CAP_FACE",FACE,{"disambiguationData":[OSD([sQuery(id+"F29.wireOp",EDGE,"E64"),sQuery(id+"F29.wireOp",EDGE,"uRIWM3SE-HjLF-7pp9-PAPw-X7moghJSHD6N"),sQuery(id+"F29.wireOp",EDGE,"OpWu1XS1-rJ0G-L7na-vCCU-mSWjQRgsFhHs"),sQuery(id+"F29.wireOp",EDGE,"5WCWpNXw-oUZq-tZ0W-K7wV-ze9KUBz3YtkG"),sQuery(id+"F29.wireOp",EDGE,"7uMPZRK7-dJ3t-dW4W-SYb4-OJ9rWrU49J69"),sQuery(id+"F29.wireOp",EDGE,"E70"),sQuery(id+"F29.wireOp",EDGE,"E71.0.1.0"),sQuery(id+"F29.wireOp",EDGE,"E71.1.0.0"),sQuery(id+"F29.wireOp",EDGE,"E71.1.1.0"),sQuery(id+"F29.wireOp",EDGE,"E71.2.0.0"),sQuery(id+"F29.wireOp",EDGE,"E71.2.1.0"),sQuery(id+"F29.wireOp",EDGE,"E72.1.0"),sQuery(id+"F29.wireOp",EDGE,"E72.1.1"),sQuery(id+"F29.wireOp",EDGE,"E72.1.2"),sQuery(id+"F29.wireOp",EDGE,"E72.1.3"),sQuery(id+"F29.wireOp",EDGE,"E72.1.4"),sQuery(id+"F29.wireOp",EDGE,"E72.1.5"),sQuery(id+"F29.wireOp",EDGE,"E72.2.0"),sQuery(id+"F29.wireOp",EDGE,"E72.2.1"),sQuery(id+"F29.wireOp",EDGE,"E72.2.2"),sQuery(id+"F29.wireOp",EDGE,"E72.2.3"),sQuery(id+"F29.wireOp",EDGE,"E72.2.4"),sQuery(id+"F29.wireOp",EDGE,"E72.2.5"),sQuery(id+"F29.wireOp",EDGE,"E72.3.0"),sQuery(id+"F29.wireOp",EDGE,"E72.3.1"),sQuery(id+"F29.wireOp",EDGE,"E72.3.2"),sQuery(id+"F29.wireOp",EDGE,"E72.3.3"),sQuery(id+"F29.wireOp",EDGE,"E72.3.4"),sQuery(id+"F29.wireOp",EDGE,"E72.3.5"),sQuery(id+"F29.wireOp",EDGE,"MWTFZZsm-TkuO-LHkw-GViv-oMLyzMMDyDRn"),sQuery(id+"F29.wireOp",EDGE,"GyXdrMyZ-hX8P-kCdx-Fy4I-smiBgP16g9wU"),sQuery(id+"F29.wireOp",EDGE,"xfPsAW4P-y80J-i8pV-4Xyk-83benEWPVPtz"),sQuery(id+"F29.wireOp",EDGE,"6Y47HZDB-cD7Z-lsIU-wivC-G1rU3xkXcbP8"),sQuery(id+"F29.wireOp",EDGE,"MsHUfoxW-e4w1-cYn7-fB64-FabNyXJABTFu"),sQuery(id+"F29.wireOp",EDGE,"AgJOStj8-b7i0-9NHD-Wp1m-9V2MUWHPPAkM"),sQuery(id+"F29.wireOp",EDGE,"2FiGOEOV-d23T-Yi4W-LUrU-KpRIATOJ68xC"),sQuery(id+"F29.wireOp",EDGE,"WGm4aKHV-mp4h-Ylfv-BJxi-OSG1QRuU1NWU"),sQuery(id+"F29.wireOp",EDGE,"cP9DnLIQ-dx8G-reGj-CAKd-0kmyXJh7Ob4g")])],"isStart":true});
            var sketch = newSketch(context, id + "F31", { "sketchPlane" : qUnion([Q0])});
            skCircle(sketch, "E76", {"center": v(0, 0) * mm, "radius": 50 * mm});
            skLineSegment(sketch, "E77", {"start": v(0, -80) * mm, "end": v(0, 80) * mm, "construction": true});
            skLineSegment(sketch, "E78", {"start": v(80, 0) * mm, "end": v(-80, 0) * mm, "construction": true});
            skLineSegment(sketch, "E79", {"start": v(47.7, -15) * mm, "end": v(80, -15) * mm});
            skLineSegment(sketch, "E80", {"start": v(15, -47.7) * mm, "end": v(15, -80) * mm});
            skLineSegment(sketch, "E81.MirrorCS", {"start": v(47.7, 15) * mm, "end": v(80, 15) * mm});
            skLineSegment(sketch, "E82.MirrorCS", {"start": v(15, 47.7) * mm, "end": v(15, 80) * mm});
            skLineSegment(sketch, "E83.MirrorCS", {"start": v(-15, -47.7) * mm, "end": v(-15, -80) * mm});
            skLineSegment(sketch, "E84.MirrorCS", {"start": v(-15, 47.7) * mm, "end": v(-15, 80) * mm});
            skLineSegment(sketch, "E85.MirrorCS", {"start": v(-47.7, 15) * mm, "end": v(-80, 15) * mm});
            skLineSegment(sketch, "E86.MirrorCS", {"start": v(-47.7, -15) * mm, "end": v(-80, -15) * mm});
            skLineSegment(sketch, "E87.bottom", {"start": v(80, -80) * mm, "end": v(-80, -80) * mm});
            skLineSegment(sketch, "E87.top", {"start": v(80, 80) * mm, "end": v(-80, 80) * mm});
            skLineSegment(sketch, "E87.left", {"start": v(80, -80) * mm, "end": v(80, 80) * mm});
            skLineSegment(sketch, "E87.right", {"start": v(-80, -80) * mm, "end": v(-80, 80) * mm});
            skSolve(sketch);
        }
        {
            var Q0;
            {var subQ0=sQuery(id+"F31.wireOp",EDGE,"E79");var subQ1=sQuery(id+"F31.wireOp",EDGE,"E76");var subQ2=makeQuery(id+"F31.imprint","INTERSECT",VERTEX,{"derivedFrom":[subQ1,subQ0]});Q0=makeQuery(id+"F31.imprint","IMPRINT",FACE,{"disambiguationData":[TD([[makeQuery(id+"F31.imprint","IMPRINT",EDGE,{"disambiguationData":[TD([[subQ2,1.0]])],"derivedFrom":subQ1}),-1.0]])]});}
            var Q1;
            {var subQ0=sQuery(id+"F31.wireOp",EDGE,"E81.MirrorCS");var subQ1=sQuery(id+"F31.wireOp",EDGE,"E76");var subQ2=makeQuery(id+"F31.imprint","INTERSECT",VERTEX,{"derivedFrom":[subQ1,subQ0]});Q1=makeQuery(id+"F31.imprint","IMPRINT",FACE,{"disambiguationData":[TD([[makeQuery(id+"F31.imprint","IMPRINT",EDGE,{"disambiguationData":[TD([[subQ2,-1.0]])],"derivedFrom":subQ1}),-1.0]])]});}
            var Q2;
            {var subQ0=sQuery(id+"F31.wireOp",EDGE,"E84.MirrorCS");var subQ1=sQuery(id+"F31.wireOp",EDGE,"E76");var subQ2=makeQuery(id+"F31.imprint","INTERSECT",VERTEX,{"derivedFrom":[subQ1,subQ0]});Q2=makeQuery(id+"F31.imprint","IMPRINT",FACE,{"disambiguationData":[TD([[makeQuery(id+"F31.imprint","IMPRINT",EDGE,{"disambiguationData":[TD([[subQ2,-1.0]])],"derivedFrom":subQ1}),-1.0]])]});}
            var Q3;
            {var subQ0=sQuery(id+"F31.wireOp",EDGE,"E83.MirrorCS");var subQ1=sQuery(id+"F31.wireOp",EDGE,"E76");var subQ2=makeQuery(id+"F31.imprint","INTERSECT",VERTEX,{"derivedFrom":[subQ1,subQ0]});Q3=makeQuery(id+"F31.imprint","IMPRINT",FACE,{"disambiguationData":[TD([[makeQuery(id+"F31.imprint","IMPRINT",EDGE,{"disambiguationData":[TD([[subQ2,1.0]])],"derivedFrom":subQ1}),-1.0]])]});}
            extrude(context, id + "F32", {"entities" : qUnion([Q0, Q1, Q2, Q3]), "operationType" : NewBodyOperationType.REMOVE, "oppositeDirection" : true, "depth" : 25 * mm});
        }
        {
            var Q0;
            Q0=makeQuery(id+"F30.opExtrude","CAP_FACE",FACE,{"disambiguationData":[OSD([sQuery(id+"F29.wireOp",EDGE,"E64"),sQuery(id+"F29.wireOp",EDGE,"uRIWM3SE-HjLF-7pp9-PAPw-X7moghJSHD6N"),sQuery(id+"F29.wireOp",EDGE,"OpWu1XS1-rJ0G-L7na-vCCU-mSWjQRgsFhHs"),sQuery(id+"F29.wireOp",EDGE,"5WCWpNXw-oUZq-tZ0W-K7wV-ze9KUBz3YtkG"),sQuery(id+"F29.wireOp",EDGE,"7uMPZRK7-dJ3t-dW4W-SYb4-OJ9rWrU49J69"),sQuery(id+"F29.wireOp",EDGE,"E70"),sQuery(id+"F29.wireOp",EDGE,"E71.0.1.0"),sQuery(id+"F29.wireOp",EDGE,"E71.1.0.0"),sQuery(id+"F29.wireOp",EDGE,"E71.1.1.0"),sQuery(id+"F29.wireOp",EDGE,"E71.2.0.0"),sQuery(id+"F29.wireOp",EDGE,"E71.2.1.0"),sQuery(id+"F29.wireOp",EDGE,"E72.1.0"),sQuery(id+"F29.wireOp",EDGE,"E72.1.1"),sQuery(id+"F29.wireOp",EDGE,"E72.1.2"),sQuery(id+"F29.wireOp",EDGE,"E72.1.3"),sQuery(id+"F29.wireOp",EDGE,"E72.1.4"),sQuery(id+"F29.wireOp",EDGE,"E72.1.5"),sQuery(id+"F29.wireOp",EDGE,"E72.2.0"),sQuery(id+"F29.wireOp",EDGE,"E72.2.1"),sQuery(id+"F29.wireOp",EDGE,"E72.2.2"),sQuery(id+"F29.wireOp",EDGE,"E72.2.3"),sQuery(id+"F29.wireOp",EDGE,"E72.2.4"),sQuery(id+"F29.wireOp",EDGE,"E72.2.5"),sQuery(id+"F29.wireOp",EDGE,"E72.3.0"),sQuery(id+"F29.wireOp",EDGE,"E72.3.1"),sQuery(id+"F29.wireOp",EDGE,"E72.3.2"),sQuery(id+"F29.wireOp",EDGE,"E72.3.3"),sQuery(id+"F29.wireOp",EDGE,"E72.3.4"),sQuery(id+"F29.wireOp",EDGE,"E72.3.5"),sQuery(id+"F29.wireOp",EDGE,"MWTFZZsm-TkuO-LHkw-GViv-oMLyzMMDyDRn"),sQuery(id+"F29.wireOp",EDGE,"GyXdrMyZ-hX8P-kCdx-Fy4I-smiBgP16g9wU"),sQuery(id+"F29.wireOp",EDGE,"xfPsAW4P-y80J-i8pV-4Xyk-83benEWPVPtz"),sQuery(id+"F29.wireOp",EDGE,"6Y47HZDB-cD7Z-lsIU-wivC-G1rU3xkXcbP8"),sQuery(id+"F29.wireOp",EDGE,"MsHUfoxW-e4w1-cYn7-fB64-FabNyXJABTFu"),sQuery(id+"F29.wireOp",EDGE,"AgJOStj8-b7i0-9NHD-Wp1m-9V2MUWHPPAkM"),sQuery(id+"F29.wireOp",EDGE,"2FiGOEOV-d23T-Yi4W-LUrU-KpRIATOJ68xC"),sQuery(id+"F29.wireOp",EDGE,"WGm4aKHV-mp4h-Ylfv-BJxi-OSG1QRuU1NWU"),sQuery(id+"F29.wireOp",EDGE,"cP9DnLIQ-dx8G-reGj-CAKd-0kmyXJh7Ob4g")])],"isStart":false});
            var sketch = newSketch(context, id + "F33", { "sketchPlane" : qUnion([Q0])});
            skCircle(sketch, "E88", {"center": v(0, 0) * mm, "radius": 50 * mm, "construction": true});
            skLineSegment(sketch, "E89", {"start": v(-10, -20) * mm, "end": v(35, -20) * mm});
            skLineSegment(sketch, "E90", {"start": v(35, -20) * mm, "end": v(35, 25) * mm});
            skLineSegment(sketch, "E91", {"start": v(35, 25) * mm, "end": v(-10, 25) * mm});
            skLineSegment(sketch, "E92", {"start": v(-10, 25) * mm, "end": v(-10, -20) * mm});
            skCircle(sketch, "E93", {"center": v(-22.7, -31.15) * mm, "radius": 1.5 * mm});
            skCircle(sketch, "E94", {"center": v(11, -31.15) * mm, "radius": 1.5 * mm});
            skSolve(sketch);
        }
        {
            var Q0;
            {var subQ2=sQuery(id+"F33.wireOp",EDGE,"91151419-da5c-4e2f-80e4-cd289c5ef62d");Q0=makeQuery(id+"F33.imprint","IMPRINT",FACE,{"disambiguationData":[TD([[makeQuery(id+"F33.imprint","IMPRINT",EDGE,{"derivedFrom":subQ2}),-1.0]])]});}
            var Q1;
            {var subQ0=sQuery(id+"F33.wireOp",EDGE,"c5d21df8-33a3-4da9-818d-4b2ae637eef0");Q1=makeQuery(id+"F33.imprint","IMPRINT",FACE,{"disambiguationData":[TD([[makeQuery(id+"F33.imprint","IMPRINT",EDGE,{"derivedFrom":subQ0}),1.0]])]});}
            var Q2;
            Q2=makeQuery(id+"F33.imprint","IMPRINT",FACE,{"disambiguationData":[TD([[makeQuery(id+"F33.imprint","IMPRINT",EDGE,{"derivedFrom":sQuery(id+"F33.wireOp",EDGE,"zmxfzKeM-U0Dl-q0yE-mnSx-mZVEBNf3zO6X.bottom")}),1.0]])]});
            var Q3;
            Q3=makeQuery(id+"F33.imprint","IMPRINT",FACE,{"disambiguationData":[TD([[makeQuery(id+"F33.imprint","IMPRINT",EDGE,{"derivedFrom":sQuery(id+"F33.wireOp",EDGE,"E89")}),1.0]])]});
            var Q4;
            Q4=makeQuery(id+"F33.imprint","IMPRINT",FACE,{"disambiguationData":[TD([[makeQuery(id+"F33.imprint","IMPRINT",EDGE,{"derivedFrom":sQuery(id+"F33.wireOp",EDGE,"E93")}),1.0]])]});
            extrude(context, id + "F34", {"entities" : qUnion([Q0, Q1, Q2, Q3, Q4]), "operationType" : NewBodyOperationType.REMOVE, "endBound" : BoundingType.THROUGH_ALL, "oppositeDirection" : true, "depth" : 25 * mm});
        }
        {
            var Q0;
            Q0=makeQuery(id+"F34.boolean.opBoolean","COPY",EDGE,{"derivedFrom":makeQuery(id+"F34.opExtrude","SWEPT_EDGE",EDGE,{"disambiguationData":[OSD([sQuery(id+"F33.wireOp",EDGE,"E91"),sQuery(id+"F33.wireOp",EDGE,"E92")])]})});
            var Q1;
            Q1=makeQuery(id+"F34.boolean.opBoolean","COPY",EDGE,{"derivedFrom":makeQuery(id+"F34.opExtrude","SWEPT_EDGE",EDGE,{"disambiguationData":[OSD([sQuery(id+"F33.wireOp",EDGE,"E90"),sQuery(id+"F33.wireOp",EDGE,"E91")])]})});
            var Q2;
            Q2=makeQuery(id+"F34.boolean.opBoolean","COPY",EDGE,{"derivedFrom":makeQuery(id+"F34.opExtrude","SWEPT_EDGE",EDGE,{"disambiguationData":[OSD([sQuery(id+"F33.wireOp",EDGE,"E89"),sQuery(id+"F33.wireOp",EDGE,"E90")])]})});
            var Q3;
            Q3=makeQuery(id+"F34.boolean.opBoolean","COPY",EDGE,{"derivedFrom":makeQuery(id+"F34.opExtrude","SWEPT_EDGE",EDGE,{"disambiguationData":[OSD([sQuery(id+"F33.wireOp",EDGE,"E89"),sQuery(id+"F33.wireOp",EDGE,"E92")])]})});
            fillet(context, id + "F35", {"entities" : qUnion([Q0, Q1, Q2, Q3]), "radius" : 10 * mm, "tangentPropagation" : true, "allowEdgeOverflow" : false});
        }
        {
            var Q0;
            Q0 = qSketchRegion(id + "F29", true);
            extrude(context, id + "F36", {"entities" : qUnion([Q0]), "oppositeDirection" : true, "depth" : 11.5 * mm, "hasSecondDirection" : true, "secondDirectionOppositeDirection" : true, "secondDirectionDepth" : 10 * mm});
        }
        {
            var Q0;
            {var subQ0=sQuery(id+"F31.wireOp",EDGE,"E81.MirrorCS");var subQ1=sQuery(id+"F31.wireOp",EDGE,"E76");var subQ2=makeQuery(id+"F31.imprint","INTERSECT",VERTEX,{"derivedFrom":[subQ1,subQ0]});Q0=makeQuery(id+"F31.imprint","IMPRINT",FACE,{"disambiguationData":[TD([[makeQuery(id+"F31.imprint","IMPRINT",EDGE,{"disambiguationData":[TD([[subQ2,-1.0]])],"derivedFrom":subQ1}),-1.0]])]});}
            var Q1;
            {var subQ0=sQuery(id+"F31.wireOp",EDGE,"E79");var subQ1=sQuery(id+"F31.wireOp",EDGE,"E76");var subQ2=makeQuery(id+"F31.imprint","INTERSECT",VERTEX,{"derivedFrom":[subQ1,subQ0]});Q1=makeQuery(id+"F31.imprint","IMPRINT",FACE,{"disambiguationData":[TD([[makeQuery(id+"F31.imprint","IMPRINT",EDGE,{"disambiguationData":[TD([[subQ2,1.0]])],"derivedFrom":subQ1}),-1.0]])]});}
            var Q2;
            {var subQ0=sQuery(id+"F31.wireOp",EDGE,"E83.MirrorCS");var subQ1=sQuery(id+"F31.wireOp",EDGE,"E76");var subQ2=makeQuery(id+"F31.imprint","INTERSECT",VERTEX,{"derivedFrom":[subQ1,subQ0]});Q2=makeQuery(id+"F31.imprint","IMPRINT",FACE,{"disambiguationData":[TD([[makeQuery(id+"F31.imprint","IMPRINT",EDGE,{"disambiguationData":[TD([[subQ2,1.0]])],"derivedFrom":subQ1}),-1.0]])]});}
            var Q3;
            {var subQ0=sQuery(id+"F31.wireOp",EDGE,"E84.MirrorCS");var subQ1=sQuery(id+"F31.wireOp",EDGE,"E76");var subQ2=makeQuery(id+"F31.imprint","INTERSECT",VERTEX,{"derivedFrom":[subQ1,subQ0]});Q3=makeQuery(id+"F31.imprint","IMPRINT",FACE,{"disambiguationData":[TD([[makeQuery(id+"F31.imprint","IMPRINT",EDGE,{"disambiguationData":[TD([[subQ2,-1.0]])],"derivedFrom":subQ1}),-1.0]])]});}
            extrude(context, id + "F37", {"entities" : qUnion([Q0, Q1, Q2, Q3]), "operationType" : NewBodyOperationType.REMOVE, "endBound" : BoundingType.THROUGH_ALL, "depth" : 25 * mm});
        }
        {
            var Q0;
            {var subQ0=sQuery(id+"F33.wireOp",EDGE,"91151419-da5c-4e2f-80e4-cd289c5ef62d");Q0=makeQuery(id+"F33.imprint","IMPRINT",FACE,{"disambiguationData":[TD([[makeQuery(id+"F33.imprint","IMPRINT",EDGE,{"derivedFrom":subQ0}),-1.0]])]});}
            var Q1;
            Q1=makeQuery(id+"F33.imprint","IMPRINT",FACE,{"disambiguationData":[TD([[makeQuery(id+"F33.imprint","IMPRINT",EDGE,{"derivedFrom":sQuery(id+"F33.wireOp",EDGE,"zmxfzKeM-U0Dl-q0yE-mnSx-mZVEBNf3zO6X.bottom")}),1.0]])]});
            var Q2;
            Q2=makeQuery(id+"F33.imprint","IMPRINT",FACE,{"disambiguationData":[TD([[makeQuery(id+"F33.imprint","IMPRINT",EDGE,{"derivedFrom":sQuery(id+"F33.wireOp",EDGE,"E89")}),1.0]])]});
            var Q3;
            Q3=makeQuery(id+"F33.imprint","IMPRINT",FACE,{"disambiguationData":[TD([[makeQuery(id+"F33.imprint","IMPRINT",EDGE,{"derivedFrom":sQuery(id+"F33.wireOp",EDGE,"E93")}),1.0]])]});
            var Q4;
            Q4=makeQuery(id+"F33.imprint","IMPRINT",FACE,{"disambiguationData":[TD([[makeQuery(id+"F33.imprint","IMPRINT",EDGE,{"derivedFrom":sQuery(id+"F33.wireOp",EDGE,"E94")}),1.0]])]});
            extrude(context, id + "F38", {"entities" : qUnion([Q0, Q1, Q2, Q3, Q4]), "operationType" : NewBodyOperationType.REMOVE, "oppositeDirection" : true, "depth" : 25 * mm});
        }
        {
            var Q0;
            Q0=makeQuery(id+"F38.boolean.opBoolean","COPY",EDGE,{"derivedFrom":makeQuery(id+"F38.opExtrude","SWEPT_EDGE",EDGE,{"disambiguationData":[OSD([sQuery(id+"F33.wireOp",EDGE,"E90"),sQuery(id+"F33.wireOp",EDGE,"E91")])]})});
            var Q1;
            Q1=makeQuery(id+"F38.boolean.opBoolean","COPY",EDGE,{"derivedFrom":makeQuery(id+"F38.opExtrude","SWEPT_EDGE",EDGE,{"disambiguationData":[OSD([sQuery(id+"F33.wireOp",EDGE,"E89"),sQuery(id+"F33.wireOp",EDGE,"E90")])]})});
            var Q2;
            Q2=makeQuery(id+"F38.boolean.opBoolean","COPY",EDGE,{"derivedFrom":makeQuery(id+"F38.opExtrude","SWEPT_EDGE",EDGE,{"disambiguationData":[OSD([sQuery(id+"F33.wireOp",EDGE,"E91"),sQuery(id+"F33.wireOp",EDGE,"E92")])]})});
            var Q3;
            Q3=makeQuery(id+"F38.boolean.opBoolean","COPY",EDGE,{"derivedFrom":makeQuery(id+"F38.opExtrude","SWEPT_EDGE",EDGE,{"disambiguationData":[OSD([sQuery(id+"F33.wireOp",EDGE,"E89"),sQuery(id+"F33.wireOp",EDGE,"E92")])]})});
            fillet(context, id + "F39", {"entities" : qUnion([Q0, Q1, Q2, Q3]), "radius" : 10 * mm, "tangentPropagation" : true, "allowEdgeOverflow" : false});
        }
        {
            var Q0;
            {var subQ0=sQuery(id+"F29.wireOp",EDGE,"E65");Q0=makeQuery(id+"F29.imprint","IMPRINT",FACE,{"disambiguationData":[TD([[makeQuery(id+"F29.imprint","IMPRINT",EDGE,{"derivedFrom":subQ0}),1.0]])]});}
            var Q1;
            {var subQ0=sQuery(id+"F29.wireOp",EDGE,"E75");Q1=makeQuery(id+"F29.imprint","IMPRINT",FACE,{"disambiguationData":[TD([[makeQuery(id+"F29.imprint","IMPRINT",EDGE,{"derivedFrom":subQ0}),1.0]])]});}
            var Q2;
            {var subQ0=sQuery(id+"F29.wireOp",EDGE,"E74");Q2=makeQuery(id+"F29.imprint","IMPRINT",FACE,{"disambiguationData":[TD([[makeQuery(id+"F29.imprint","IMPRINT",EDGE,{"derivedFrom":subQ0}),-1.0]])]});}
            extrude(context, id + "F40", {"entities" : qUnion([Q0, Q1, Q2]), "endBound" : BoundingType.SYMMETRIC, "depth" : 12 * mm});
        }
        {
            var Q0;
            Q0=makeQuery(id+"F40.opExtrude","SWEPT_FACE",FACE,{"disambiguationData":[OSD([sQuery(id+"F29.wireOp",EDGE,"E66")])]});
            var sketch = newSketch(context, id + "F41", { "sketchPlane" : qUnion([Q0])});
            skCircle(sketch, "E95", {"center": v(0, 0) * mm, "radius": 5 * mm});
            skSolve(sketch);
        }
        {
            var Q0;
            Q0=makeQuery(id+"F41.imprint","IMPRINT",FACE,{"disambiguationData":[TD([[makeQuery(id+"F41.imprint","IMPRINT",EDGE,{"derivedFrom":sQuery(id+"F41.wireOp",EDGE,"E95")}),1.0]])]});
            var Q1;
            Q1=makeQuery(id+"F40.opExtrude","SWEPT_FACE",FACE,{"disambiguationData":[OSD([sQuery(id+"F29.wireOp",EDGE,"E73.top")])]});
            extrude(context, id + "F42", {"entities" : qUnion([Q0]), "operationType" : NewBodyOperationType.REMOVE, "endBound" : BoundingType.UP_TO_SURFACE, "oppositeDirection" : true, "endBoundEntityFace" : qUnion([Q1]), "depth" : 25 * mm});
        }
        {
            var Q0;
            Q0=qCreatedBy(makeId("Front.planeOp"),FACE);
            var sketch = newSketch(context, id + "F43", { "sketchPlane" : qUnion([Q0])});
            skLineSegment(sketch, "E96", {"start": v(-84.44, -44.72) * mm, "end": v(-84.44, -42.02) * mm});
            skLineSegment(sketch, "E97", {"start": v(-84.44, -44.72) * mm, "end": v(-84.44, -41.72) * mm});
            skPoint(sketch, "E97.endSnap0", {"position": v(-84.44, -43.37) * mm});
            skLineSegment(sketch, "E98", {"start": v(-84.44, -41.72) * mm, "end": v(-82.44, -41.72) * mm});
            skLineSegment(sketch, "E99", {"start": v(-82.44, -41.72) * mm, "end": v(-82.44, -40.72) * mm});
            skLineSegment(sketch, "E100", {"start": v(-82.44, -40.72) * mm, "end": v(-96.94, -40.72) * mm});
            skLineSegment(sketch, "E101", {"start": v(-96.94, -40.72) * mm, "end": v(-96.94, -42.52) * mm});
            skLineSegment(sketch, "E102", {"start": v(-96.94, -42.52) * mm, "end": v(-85.2, -42.52) * mm});
            skLineSegment(sketch, "E103", {"start": v(-85.2, -42.52) * mm, "end": v(-85.2, -44.72) * mm});
            skLineSegment(sketch, "E104", {"start": v(-85.2, -44.72) * mm, "end": v(-84.44, -44.72) * mm});
            skSolve(sketch);
        }
        {
            var Q0;
            {var subQ0=sQuery(id+"F43.wireOp",EDGE,"E98");Q0=makeQuery(id+"F43.imprint","IMPRINT",FACE,{"disambiguationData":[TD([[makeQuery(id+"F43.imprint","IMPRINT",EDGE,{"derivedFrom":subQ0}),1.0]])]});}
            var Q1;
            Q1=sQuery(id+"F43.wireOp",EDGE,"E99");
            revolve(context, id + "F44", {"entities" : qUnion([Q0]), "axis" : qUnion([Q1]), "revolveType" : RevolveType.FULL});
        }
        {
            var Q0;
            Q0=makeQuery(id+"F44.opRevolve","SWEPT_FACE",FACE,{"disambiguationData":[OSD([sQuery(id+"F43.wireOp",EDGE,"E100")])]});
            var sketch = newSketch(context, id + "F45", { "sketchPlane" : qUnion([Q0])});
            skCircle(sketch, "E105", {"center": v(-82.44, 0) * mm, "radius": 3 * mm});
            skCircle(sketch, "E106", {"center": v(-94.44, 0) * mm, "radius": 2.5 * mm});
            skCircle(sketch, "E107", {"center": v(-70.44, 0) * mm, "radius": 2.5 * mm});
            skLineSegment(sketch, "E108", {"start": v(-94.54, 2.5) * mm, "end": v(-82.57, 3) * mm});
            skLineSegment(sketch, "E109", {"start": v(-70.34, 2.5) * mm, "end": v(-82.32, 3) * mm});
            skLineSegment(sketch, "E110", {"start": v(-94.54, -2.5) * mm, "end": v(-82.57, -3) * mm});
            skLineSegment(sketch, "E111", {"start": v(-70.34, -2.5) * mm, "end": v(-82.32, -3) * mm});
            skCircle(sketch, "E112", {"center": v(-82.44, 0) * mm, "radius": 14.5 * mm});
            skSolve(sketch);
        }
        {
            var Q0;
            {var subQ0=sQuery(id+"F45.wireOp",EDGE,"E108");Q0=makeQuery(id+"F45.imprint","IMPRINT",FACE,{"disambiguationData":[TD([[makeQuery(id+"F45.imprint","IMPRINT",EDGE,{"derivedFrom":subQ0}),1.0]])]});}
            var Q1;
            {var subQ0=sQuery(id+"F45.wireOp",EDGE,"E110");Q1=makeQuery(id+"F45.imprint","IMPRINT",FACE,{"disambiguationData":[TD([[makeQuery(id+"F45.imprint","IMPRINT",EDGE,{"derivedFrom":subQ0}),-1.0]])]});}
            extrude(context, id + "F46", {"entities" : qUnion([Q0, Q1]), "operationType" : NewBodyOperationType.REMOVE, "oppositeDirection" : true, "depth" : 25 * mm});
        }
        {
            var Q0;
            Q0=makeQuery(id+"F37.boolean.opBoolean","COPY",EDGE,{"derivedFrom":makeQuery(id+"F37.opExtrude","SWEPT_EDGE",EDGE,{"disambiguationData":[OSD([sQuery(id+"F31.wireOp",EDGE,"E76"),sQuery(id+"F31.wireOp",EDGE,"E81.MirrorCS")])]})});
            var Q1;
            Q1=makeQuery(id+"F37.boolean.opBoolean","COPY",EDGE,{"derivedFrom":makeQuery(id+"F37.opExtrude","SWEPT_EDGE",EDGE,{"disambiguationData":[OSD([sQuery(id+"F31.wireOp",EDGE,"E76"),sQuery(id+"F31.wireOp",EDGE,"E79")])]})});
            var Q2;
            Q2=makeQuery(id+"F37.boolean.opBoolean","COPY",EDGE,{"derivedFrom":makeQuery(id+"F37.opExtrude","SWEPT_EDGE",EDGE,{"disambiguationData":[OSD([sQuery(id+"F31.wireOp",EDGE,"E76"),sQuery(id+"F31.wireOp",EDGE,"E80")])]})});
            var Q3;
            Q3=makeQuery(id+"F37.boolean.opBoolean","COPY",EDGE,{"derivedFrom":makeQuery(id+"F37.opExtrude","SWEPT_EDGE",EDGE,{"disambiguationData":[OSD([sQuery(id+"F31.wireOp",EDGE,"E76"),sQuery(id+"F31.wireOp",EDGE,"E83.MirrorCS")])]})});
            var Q4;
            Q4=makeQuery(id+"F37.boolean.opBoolean","COPY",EDGE,{"derivedFrom":makeQuery(id+"F37.opExtrude","SWEPT_EDGE",EDGE,{"disambiguationData":[OSD([sQuery(id+"F31.wireOp",EDGE,"E76"),sQuery(id+"F31.wireOp",EDGE,"E86.MirrorCS")])]})});
            var Q5;
            Q5=makeQuery(id+"F37.boolean.opBoolean","COPY",EDGE,{"derivedFrom":makeQuery(id+"F37.opExtrude","SWEPT_EDGE",EDGE,{"disambiguationData":[OSD([sQuery(id+"F31.wireOp",EDGE,"E76"),sQuery(id+"F31.wireOp",EDGE,"E85.MirrorCS")])]})});
            var Q6;
            Q6=makeQuery(id+"F37.boolean.opBoolean","COPY",EDGE,{"derivedFrom":makeQuery(id+"F37.opExtrude","SWEPT_EDGE",EDGE,{"disambiguationData":[OSD([sQuery(id+"F31.wireOp",EDGE,"E76"),sQuery(id+"F31.wireOp",EDGE,"E84.MirrorCS")])]})});
            var Q7;
            Q7=makeQuery(id+"F37.boolean.opBoolean","COPY",EDGE,{"derivedFrom":makeQuery(id+"F37.opExtrude","SWEPT_EDGE",EDGE,{"disambiguationData":[OSD([sQuery(id+"F31.wireOp",EDGE,"E76"),sQuery(id+"F31.wireOp",EDGE,"E82.MirrorCS")])]})});
            fillet(context, id + "F47", {"entities" : qUnion([Q0, Q1, Q2, Q3, Q4, Q5, Q6, Q7]), "radius" : 5 * mm, "tangentPropagation" : true, "allowEdgeOverflow" : false});
        }
        {
            var Q0;
            {var subQ0=sQuery(id+"F14.wireOp",EDGE,"E21.left");Q0=makeQuery(id+"F15.opExtrude","SWEPT_FACE",FACE,{"disambiguationData":[OSD([subQ0]),TDD([makeQuery(id+"F14.imprint","IMPRINT",EDGE,{"disambiguationData":[TD([[makeQuery(id+"F14.imprint","INTERSECT",VERTEX,{"derivedFrom":[sQuery(id+"F14.wireOp",EDGE,"E21.top"),subQ0]}),1.0]])],"derivedFrom":subQ0})])]});}
            var sketch = newSketch(context, id + "F48", { "sketchPlane" : qUnion([Q0])});
            skLineSegment(sketch, "E113", {"start": v(1.22, -31.5) * mm, "end": v(-8.78, -31.5) * mm});
            skLineSegment(sketch, "E114", {"start": v(-8.78, -31.5) * mm, "end": v(-8.78, -41.5) * mm});
            skLineSegment(sketch, "E115", {"start": v(-8.78, -41.5) * mm, "end": v(-6.78, -41.5) * mm});
            skLineSegment(sketch, "E116", {"start": v(-6.78, -41.5) * mm, "end": v(-6.78, -33.5) * mm});
            skLineSegment(sketch, "E117", {"start": v(-6.78, -33.5) * mm, "end": v(1.22, -33.5) * mm});
            skLineSegment(sketch, "E118", {"start": v(1.22, -33.5) * mm, "end": v(1.22, -31.5) * mm});
            skSolve(sketch);
        }
        {
            var Q0;
            {var subQ1=sQuery(id+"F48.wireOp",EDGE,"E114");Q0=makeQuery(id+"F48.imprint","IMPRINT",FACE,{"disambiguationData":[TD([[makeQuery(id+"F48.imprint","IMPRINT",EDGE,{"derivedFrom":subQ1}),1.0]])]});}
            var Q1;
            {var subQ0=sQuery(id+"F48.wireOp",EDGE,"E118");Q1=makeQuery(id+"F48.imprint","IMPRINT",FACE,{"disambiguationData":[TD([[makeQuery(id+"F48.imprint","IMPRINT",EDGE,{"derivedFrom":subQ0}),1.0]])]});}
            extrude(context, id + "F49", {"entities" : qUnion([Q0, Q1]), "depth" : 10 * mm});
        }
        {
            var Q0;
            Q0=makeQuery(id+"F49.opExtrude","SWEPT_FACE",FACE,{"disambiguationData":[OSD([sQuery(id+"F48.wireOp",EDGE,"E117")])]});
            var sketch = newSketch(context, id + "F50", { "sketchPlane" : qUnion([Q0])});
            skCircle(sketch, "E119", {"center": v(-19.95, -2.78) * mm, "radius": 1.25 * mm});
            skSolve(sketch);
        }
        {
            var Q0;
            Q0=makeQuery(id+"F50.imprint","IMPRINT",FACE,{"disambiguationData":[TD([[makeQuery(id+"F50.imprint","IMPRINT",EDGE,{"derivedFrom":sQuery(id+"F50.wireOp",EDGE,"E119")}),1.0]])]});
            extrude(context, id + "F51", {"entities" : qUnion([Q0]), "operationType" : NewBodyOperationType.REMOVE, "oppositeDirection" : true, "depth" : 25 * mm});
        }
        {
            var Q0;
            Q0=makeQuery(id+"F49.opExtrude","SWEPT_FACE",FACE,{"disambiguationData":[OSD([sQuery(id+"F48.wireOp",EDGE,"E116")])]});
            var sketch = newSketch(context, id + "F52", { "sketchPlane" : qUnion([Q0])});
            skCircle(sketch, "E120", {"center": v(-22.45, -36.5) * mm, "radius": 1.5 * mm});
            skSolve(sketch);
        }
        {
            var Q0;
            Q0=makeQuery(id+"F52.imprint","IMPRINT",FACE,{"disambiguationData":[TD([[makeQuery(id+"F52.imprint","IMPRINT",EDGE,{"derivedFrom":sQuery(id+"F52.wireOp",EDGE,"E120")}),1.0]])]});
            extrude(context, id + "F53", {"entities" : qUnion([Q0]), "operationType" : NewBodyOperationType.REMOVE, "oppositeDirection" : true, "depth" : 25 * mm});
        }
        {
            var Q0;
            Q0=makeQuery(id+"F49.opExtrude","SWEPT_BODY",BODY,{"disambiguationData":[OSD([sQuery(id+"F48.wireOp",EDGE,"E113"),sQuery(id+"F48.wireOp",EDGE,"E114"),sQuery(id+"F48.wireOp",EDGE,"E115"),sQuery(id+"F48.wireOp",EDGE,"E116"),sQuery(id+"F48.wireOp",EDGE,"E117"),sQuery(id+"F48.wireOp",EDGE,"E118")])]});
            var Q1;
            Q1=makeQuery(id+"F49.opExtrude","SWEPT_EDGE",EDGE,{"disambiguationData":[OSD([sQuery(id+"F48.wireOp",EDGE,"E113"),sQuery(id+"F48.wireOp",EDGE,"E118")])]});
            transform(context, id + "F54", {"entities" : qUnion([Q0]), "transformType" : TransformType.ROTATION, "transformAxis" : qUnion([Q1]), "angle" : 90 * degree, "oppositeDirection" : true, "makeCopy" : false});
        }
        {
            var Q0;
            Q0=makeQuery(id+"F49.opExtrude","SWEPT_BODY",BODY,{"disambiguationData":[OSD([sQuery(id+"F48.wireOp",EDGE,"E113"),sQuery(id+"F48.wireOp",EDGE,"E114"),sQuery(id+"F48.wireOp",EDGE,"E115"),sQuery(id+"F48.wireOp",EDGE,"E116"),sQuery(id+"F48.wireOp",EDGE,"E117"),sQuery(id+"F48.wireOp",EDGE,"E118")])]});
            var Q1;
            Q1=qCreatedBy(makeId("Right.planeOp"),FACE);
            mirror(context, id + "F55", {"entities" : qUnion([Q0]), "mirrorPlane" : qUnion([Q1])});
        }
    });
